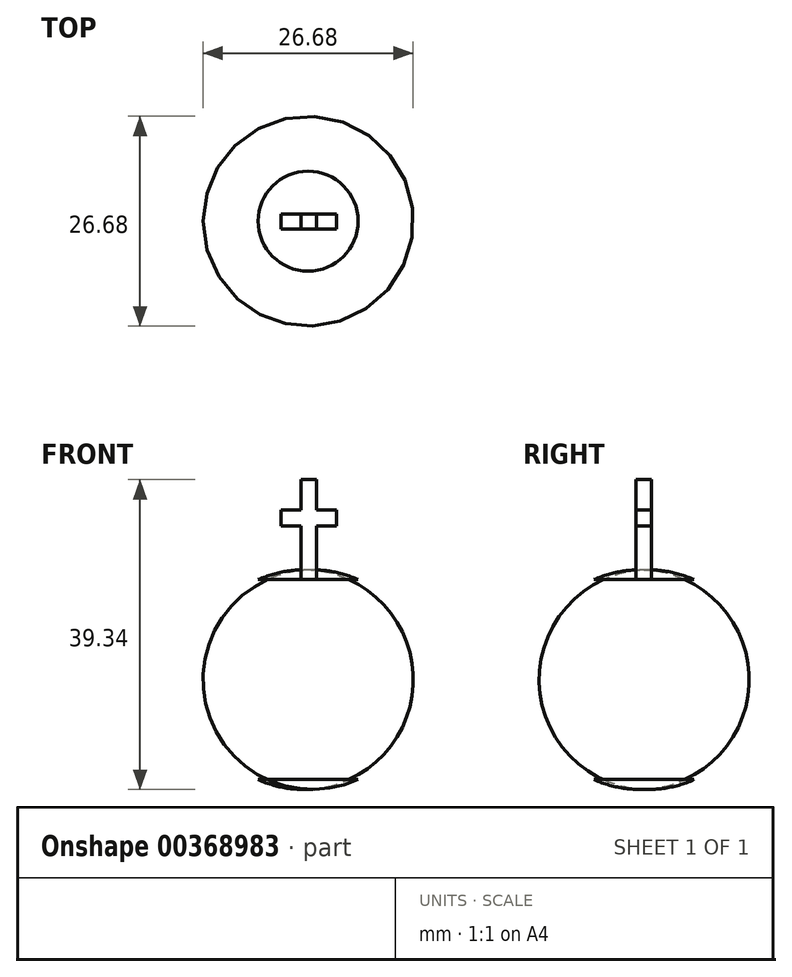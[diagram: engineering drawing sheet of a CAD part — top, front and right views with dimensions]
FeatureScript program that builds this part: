
annotation { "Feature Type Name" : "Feature", "Feature Type Description" : "" }
export const myFeature = defineFeature(function(context is Context, id is Id, definition is map)
    precondition{}
    {
        {
            var Q0;
            Q0=qCreatedBy(makeId("Front.planeOp"),FACE);
            var sketch = newSketch(context, id + "F0", { "sketchPlane" : qUnion([Q0])});
            skLineSegment(sketch, "E0", {"start": v(0, -12.02) * mm, "end": v(0, -37.42) * mm});
            skLineSegment(sketch, "E1", {"start": v(0, -37.42) * mm, "end": v(-6.35, -37.42) * mm});
            skLineSegment(sketch, "E2", {"start": v(0, -12.02) * mm, "end": v(-6.35, -12.02) * mm});
            skArc(sketch, "E3", {"start": v(-6.35, -12.02) * mm, "mid": v(-14.54, -24.72) * mm, "end": v(-6.35, -37.42) * mm});
            skSolve(sketch);
        }
        {
            var Q0;
            Q0=makeQuery(id+"F0.imprint","IMPRINT",FACE,{"disambiguationData":[TD([[makeQuery(id+"F0.imprint","IMPRINT",EDGE,{"derivedFrom":sQuery(id+"F0.wireOp",EDGE,"E0")}),-1.0]])]});
            var Q1;
            Q1=sQuery(id+"F0.wireOp",EDGE,"E0");
            revolve(context, id + "F1", {"entities" : qUnion([Q0]), "axis" : qUnion([Q1]), "revolveType" : RevolveType.FULL});
        }
        {
            var Q0;
            Q0=makeQuery(id+"F1.opRevolve","SWEPT_FACE",FACE,{"disambiguationData":[OSD([sQuery(id+"F0.wireOp",EDGE,"E2")])]});
            var sketch = newSketch(context, id + "F2", { "sketchPlane" : qUnion([Q0])});
            skLineSegment(sketch, "E4.bottom", {"start": v(-0.87, -1.03) * mm, "end": v(1.06, -1.03) * mm});
            skLineSegment(sketch, "E4.top", {"start": v(-0.87, 0.9) * mm, "end": v(1.06, 0.9) * mm});
            skLineSegment(sketch, "E4.left", {"start": v(-0.87, -1.03) * mm, "end": v(-0.87, 0.9) * mm});
            skLineSegment(sketch, "E4.right", {"start": v(1.06, -1.03) * mm, "end": v(1.06, 0.9) * mm});
            skSolve(sketch);
        }
        {
            var Q0;
            Q0=makeQuery(id+"F2.imprint","IMPRINT",FACE,{"disambiguationData":[TD([[makeQuery(id+"F2.imprint","IMPRINT",EDGE,{"derivedFrom":sQuery(id+"F2.wireOp",EDGE,"E4.bottom")}),1.0]])]});
            extrude(context, id + "F3", {"entities" : qUnion([Q0]), "operationType" : NewBodyOperationType.ADD, "depth" : 12.7 * mm});
        }
        {
            var Q0;
            {var subQ0=sQuery(id+"F2.wireOp",EDGE,"E4.top");Q0=makeQuery(id+"FZ6gsioT5ROSc5m_1.boolean.opBoolean","MERGE",FACE,{"derivedFrom":[makeQuery(id+"F3.opExtrude","SWEPT_FACE",FACE,{"disambiguationData":[OSD([subQ0])]}),makeQuery(id+"FZ6gsioT5ROSc5m_1.opExtrude","CAP_FACE",FACE,{"disambiguationData":[OSD([subQ0,sQuery(id+"F2.wireOp",EDGE,"E4.right"),sQuery(id+"FpxB2Wnb8fIg0R3_1.wireOp",EDGE,"2OXYWl0r-OBZp-rjRK-gpGp-nIuAi4a2l4af.bottom"),sQuery(id+"FpxB2Wnb8fIg0R3_1.wireOp",EDGE,"2OXYWl0r-OBZp-rjRK-gpGp-nIuAi4a2l4af.top"),sQuery(id+"FpxB2Wnb8fIg0R3_1.wireOp",EDGE,"2OXYWl0r-OBZp-rjRK-gpGp-nIuAi4a2l4af.left")])],"isStart":true})]});}
            var sketch = newSketch(context, id + "F4", { "sketchPlane" : qUnion([Q0])});
            skLineSegment(sketch, "E5.bottom", {"start": v(0.87, -3.17) * mm, "end": v(3.41, -3.17) * mm});
            skLineSegment(sketch, "E5.top", {"start": v(0.87, -5.22) * mm, "end": v(3.41, -5.22) * mm});
            skLineSegment(sketch, "E5.left", {"start": v(0.87, -3.17) * mm, "end": v(0.87, -5.22) * mm});
            skLineSegment(sketch, "E5.right", {"start": v(3.41, -3.17) * mm, "end": v(3.41, -5.22) * mm});
            skSolve(sketch);
        }
        {
            var Q0;
            Q0=makeQuery(id+"F4.imprint","IMPRINT",FACE,{"disambiguationData":[TD([[makeQuery(id+"F4.imprint","IMPRINT",EDGE,{"derivedFrom":sQuery(id+"F4.wireOp",EDGE,"E5.bottom")}),-1.0]])]});
            extrude(context, id + "F5", {"entities" : qUnion([Q0]), "operationType" : NewBodyOperationType.ADD, "oppositeDirection" : true, "depth" : 1.93 * mm});
        }
        {
            var Q0;
            Q0=makeQuery(id+"F3.opExtrude","SWEPT_FACE",FACE,{"disambiguationData":[OSD([sQuery(id+"F2.wireOp",EDGE,"E4.bottom")])]});
            var sketch = newSketch(context, id + "F6", { "sketchPlane" : qUnion([Q0])});
            skLineSegment(sketch, "E6.bottom", {"start": v(3.6, -3.17) * mm, "end": v(1.06, -3.17) * mm});
            skLineSegment(sketch, "E6.top", {"start": v(3.6, -5.22) * mm, "end": v(1.06, -5.22) * mm});
            skLineSegment(sketch, "E6.left", {"start": v(3.6, -3.17) * mm, "end": v(3.6, -5.22) * mm});
            skLineSegment(sketch, "E6.right", {"start": v(1.06, -3.17) * mm, "end": v(1.06, -5.22) * mm});
            skSolve(sketch);
        }
        {
            var Q0;
            Q0 = qSketchRegion(id + "F6", true);
            extrude(context, id + "F7", {"entities" : qUnion([Q0]), "operationType" : NewBodyOperationType.ADD, "oppositeDirection" : true, "depth" : 1.93 * mm});
        }
    });
